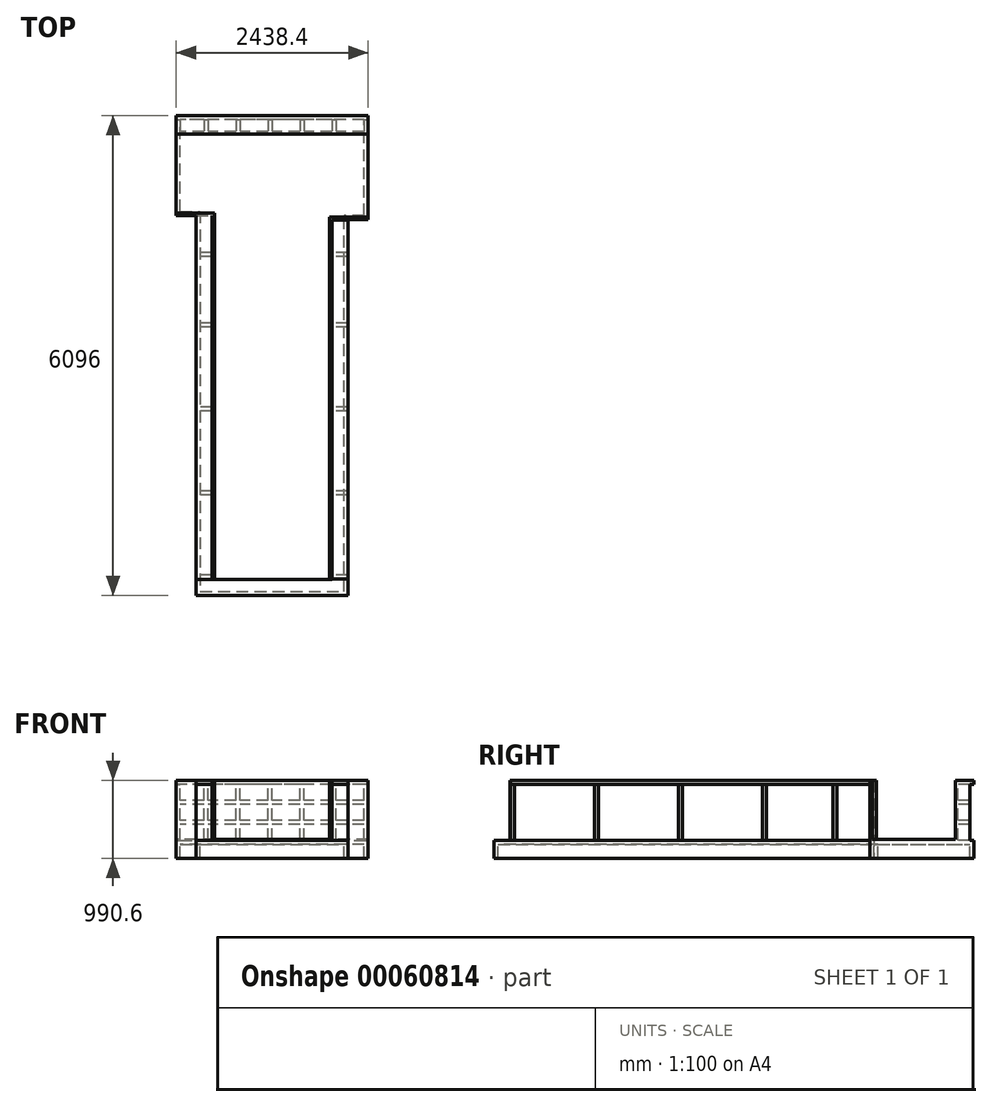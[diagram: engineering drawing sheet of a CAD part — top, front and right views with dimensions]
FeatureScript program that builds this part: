
annotation { "Feature Type Name" : "Feature", "Feature Type Description" : "" }
export const myFeature = defineFeature(function(context is Context, id is Id, definition is map)
    precondition{}
    {
        {
            var Q0;
            Q0=qCreatedBy(makeId("Top.planeOp"),FACE);
            var sketch = newSketch(context, id + "F0", { "sketchPlane" : qUnion([Q0])});
            skLineSegment(sketch, "E0", {"start": v(-1257.09, 0) * mm, "end": v(-1257.09, 1066.8) * mm});
            skLineSegment(sketch, "E1", {"start": v(-1257.09, 1066.8) * mm, "end": v(1181.31, 1066.8) * mm});
            skLineSegment(sketch, "E2", {"start": v(1181.31, 1066.8) * mm, "end": v(1181.31, -50.8) * mm});
            skLineSegment(sketch, "E3", {"start": v(1181.31, -50.8) * mm, "end": v(724.11, -50.8) * mm});
            skLineSegment(sketch, "E4", {"start": v(724.11, -50.8) * mm, "end": v(724.11, -4622.8) * mm});
            skLineSegment(sketch, "E5", {"start": v(724.11, -4622.8) * mm, "end": v(-799.89, -4622.8) * mm});
            skLineSegment(sketch, "E6", {"start": v(-1257.09, 0) * mm, "end": v(-799.89, 0) * mm});
            skLineSegment(sketch, "E7", {"start": v(-799.89, 0) * mm, "end": v(-799.89, -4622.8) * mm});
            skSolve(sketch);
        }
        {
            var Q0;
            Q0=qSketchRegion(id+"F0",true);
            extrude(context, id + "F1", {"entities" : qUnion([Q0]), "depth" : 12.7 * mm});
        }
        {
            var Q0;
            Q0=makeQuery(id+"F1.opExtrude","CAP_FACE",FACE,{"disambiguationData":[OSD([sQuery(id+"F0.wireOp",EDGE,"E0"),sQuery(id+"F0.wireOp",EDGE,"E1"),sQuery(id+"F0.wireOp",EDGE,"E2"),sQuery(id+"F0.wireOp",EDGE,"E3"),sQuery(id+"F0.wireOp",EDGE,"E4"),sQuery(id+"F0.wireOp",EDGE,"E5"),sQuery(id+"F0.wireOp",EDGE,"E6"),sQuery(id+"F0.wireOp",EDGE,"E7")])],"isStart":false});
            var sketch = newSketch(context, id + "F2", { "sketchPlane" : qUnion([Q0])});
            skLineSegment(sketch, "E8.0", {"start": v(-768.14, 31.75) * mm, "end": v(-1225.34, 31.75) * mm});
            skLineSegment(sketch, "E8.1", {"start": v(-768.14, -4591.05) * mm, "end": v(-768.14, 31.75) * mm});
            skLineSegment(sketch, "E8.2", {"start": v(-1225.34, 1035.05) * mm, "end": v(-1225.34, 31.75) * mm});
            skLineSegment(sketch, "E8.3", {"start": v(-768.14, -4591.05) * mm, "end": v(692.36, -4591.05) * mm});
            skLineSegment(sketch, "E8.4", {"start": v(1149.56, 1035.05) * mm, "end": v(-1225.34, 1035.05) * mm});
            skLineSegment(sketch, "E8.5", {"start": v(1149.56, -19.05) * mm, "end": v(1149.56, 1035.05) * mm});
            skLineSegment(sketch, "E8.6", {"start": v(692.36, -19.05) * mm, "end": v(1149.56, -19.05) * mm});
            skLineSegment(sketch, "E8.7", {"start": v(692.36, -4591.05) * mm, "end": v(692.36, -19.05) * mm});
            skLineSegment(sketch, "E9.0", {"start": v(-1257.09, 1066.8) * mm, "end": v(-1257.09, 0) * mm});
            skLineSegment(sketch, "E10.0", {"start": v(-799.89, 0) * mm, "end": v(-1257.09, 0) * mm});
            skLineSegment(sketch, "E11.0", {"start": v(-799.89, -4622.8) * mm, "end": v(-799.89, 0) * mm});
            skLineSegment(sketch, "E12.0", {"start": v(-799.89, -4622.8) * mm, "end": v(724.11, -4622.8) * mm});
            skLineSegment(sketch, "E13.0", {"start": v(724.11, -4622.8) * mm, "end": v(724.11, -50.8) * mm});
            skLineSegment(sketch, "E14.0", {"start": v(724.11, -50.8) * mm, "end": v(1181.31, -50.8) * mm});
            skLineSegment(sketch, "E15.0", {"start": v(1181.31, -50.8) * mm, "end": v(1181.31, 1066.8) * mm});
            skLineSegment(sketch, "E16.0", {"start": v(1181.31, 1066.8) * mm, "end": v(-1257.09, 1066.8) * mm});
            skSolve(sketch);
        }
        {
            var Q0;
            Q0=makeQuery(id+"F2.imprint","IMPRINT",FACE,{"disambiguationData":[TD([[makeQuery(id+"F2.imprint","IMPRINT",EDGE,{"derivedFrom":sQuery(id+"F2.wireOp",EDGE,"E8.0")}),1.0]])]});
            extrude(context, id + "F3", {"entities" : qUnion([Q0]), "operationType" : NewBodyOperationType.ADD, "depth" : 749.3 * mm});
        }
        {
            var Q0;
            Q0=makeQuery(id+"F0.imprint","IMPRINT",FACE,{"disambiguationData":[TD([[makeQuery(id+"F0.imprint","IMPRINT",EDGE,{"derivedFrom":sQuery(id+"F0.wireOp",EDGE,"E0")}),-1.0]])]});
            var sketch = newSketch(context, id + "F4", { "sketchPlane" : qUnion([Q0])});
            skLineSegment(sketch, "E17", {"start": v(927.31, -4826) * mm, "end": v(927.31, -50.8) * mm});
            skLineSegment(sketch, "E18", {"start": v(927.31, 1270) * mm, "end": v(-1003.09, 1270) * mm});
            skLineSegment(sketch, "E19", {"start": v(-1003.09, 0) * mm, "end": v(-1003.09, -4826) * mm});
            skLineSegment(sketch, "E20", {"start": v(-1003.09, -4826) * mm, "end": v(927.31, -4826) * mm});
            skLineSegment(sketch, "E21", {"start": v(-1003.09, 0) * mm, "end": v(-1257.09, 0) * mm});
            skLineSegment(sketch, "E22", {"start": v(-1257.09, 0) * mm, "end": v(-1257.09, 1270) * mm});
            skLineSegment(sketch, "E23", {"start": v(-1257.09, 1270) * mm, "end": v(-1003.09, 1270) * mm});
            skLineSegment(sketch, "E24", {"start": v(927.31, -50.8) * mm, "end": v(1181.31, -50.8) * mm});
            skLineSegment(sketch, "E25", {"start": v(1181.31, -50.8) * mm, "end": v(1181.31, 1270) * mm});
            skLineSegment(sketch, "E26", {"start": v(1181.31, 1270) * mm, "end": v(927.31, 1270) * mm});
            skSolve(sketch);
        }
        {
            var Q0;
            Q0=qSketchRegion(id+"F4",true);
            extrude(context, id + "F5", {"entities" : qUnion([Q0]), "operationType" : NewBodyOperationType.ADD, "oppositeDirection" : true, "depth" : 50.8 * mm});
        }
        {
            var Q0;
            Q0=makeQuery(id+"F3.boolean.opBoolean","MERGE",FACE,{"derivedFrom":[makeQuery(id+"F1.opExtrude","SWEPT_FACE",FACE,{"disambiguationData":[OSD([sQuery(id+"F0.wireOp",EDGE,"E1")])]}),makeQuery(id+"F3.opExtrude","SWEPT_FACE",FACE,{"disambiguationData":[OSD([sQuery(id+"F2.wireOp",EDGE,"E16.0")])]})]});
            var sketch = newSketch(context, id + "F6", { "sketchPlane" : qUnion([Q0])});
            skLineSegment(sketch, "E27.bottom", {"start": v(-1181.31, 0) * mm, "end": v(-1130.51, 0) * mm});
            skLineSegment(sketch, "E27.top", {"start": v(-1181.31, 711.2) * mm, "end": v(-1130.51, 711.2) * mm});
            skLineSegment(sketch, "E27.left", {"start": v(-1181.31, 0) * mm, "end": v(-1181.31, 711.2) * mm});
            skLineSegment(sketch, "E27.right", {"start": v(-1130.51, 0) * mm, "end": v(-1130.51, 203.2) * mm});
            skLineSegment(sketch, "E28.1.0.0", {"start": v(-774.91, 0) * mm, "end": v(-774.91, 203.2) * mm});
            skLineSegment(sketch, "E28.1.0.1", {"start": v(-724.11, 0) * mm, "end": v(-724.11, 203.2) * mm});
            skLineSegment(sketch, "E28.1.0.2", {"start": v(-774.91, 711.2) * mm, "end": v(-724.11, 711.2) * mm});
            skLineSegment(sketch, "E28.1.0.3", {"start": v(-774.91, 0) * mm, "end": v(-724.11, 0) * mm});
            skLineSegment(sketch, "E28.2.0.0", {"start": v(-368.51, 0) * mm, "end": v(-368.51, 203.2) * mm});
            skLineSegment(sketch, "E28.2.0.1", {"start": v(-317.71, 0) * mm, "end": v(-317.71, 203.2) * mm});
            skLineSegment(sketch, "E28.2.0.2", {"start": v(-368.51, 711.2) * mm, "end": v(-317.71, 711.2) * mm});
            skLineSegment(sketch, "E28.2.0.3", {"start": v(-368.51, 0) * mm, "end": v(-317.71, 0) * mm});
            skLineSegment(sketch, "E28.3.0.0", {"start": v(37.89, 0) * mm, "end": v(37.89, 203.2) * mm});
            skLineSegment(sketch, "E28.3.0.1", {"start": v(88.69, 0) * mm, "end": v(88.69, 203.2) * mm});
            skLineSegment(sketch, "E28.3.0.2", {"start": v(37.89, 711.2) * mm, "end": v(88.69, 711.2) * mm});
            skLineSegment(sketch, "E28.3.0.3", {"start": v(37.89, 0) * mm, "end": v(88.69, 0) * mm});
            skLineSegment(sketch, "E28.4.0.0", {"start": v(444.29, 0) * mm, "end": v(444.29, 203.2) * mm});
            skLineSegment(sketch, "E28.4.0.1", {"start": v(495.09, 0) * mm, "end": v(495.09, 203.2) * mm});
            skLineSegment(sketch, "E28.4.0.2", {"start": v(444.29, 711.2) * mm, "end": v(495.09, 711.2) * mm});
            skLineSegment(sketch, "E28.4.0.3", {"start": v(444.29, 0) * mm, "end": v(495.09, 0) * mm});
            skLineSegment(sketch, "E28.5.0.0", {"start": v(850.69, 0) * mm, "end": v(850.69, 203.2) * mm});
            skLineSegment(sketch, "E28.5.0.1", {"start": v(901.49, 0) * mm, "end": v(901.49, 203.2) * mm});
            skLineSegment(sketch, "E28.5.0.2", {"start": v(850.69, 711.2) * mm, "end": v(901.49, 711.2) * mm});
            skLineSegment(sketch, "E28.5.0.3", {"start": v(850.69, 0) * mm, "end": v(901.49, 0) * mm});
            skLineSegment(sketch, "E28.direction1", {"start": v(-1181.31, 0) * mm, "end": v(-774.91, 0) * mm, "construction": true});
            skLineSegment(sketch, "E29.bottom", {"start": v(1257.09, 0) * mm, "end": v(1206.29, 0) * mm});
            skLineSegment(sketch, "E29.top", {"start": v(1257.09, 711.2) * mm, "end": v(1206.29, 711.2) * mm});
            skLineSegment(sketch, "E29.left", {"start": v(1257.09, 0) * mm, "end": v(1257.09, 711.2) * mm});
            skLineSegment(sketch, "E29.right", {"start": v(1206.29, 0) * mm, "end": v(1206.29, 203.2) * mm});
            skLineSegment(sketch, "E30.bottom", {"start": v(-1130.51, 254) * mm, "end": v(-774.91, 254) * mm});
            skLineSegment(sketch, "E30.top", {"start": v(-1130.51, 203.2) * mm, "end": v(-774.91, 203.2) * mm});
            skLineSegment(sketch, "E30.left", {"start": v(-1181.31, 254) * mm, "end": v(-1181.31, 203.2) * mm});
            skLineSegment(sketch, "E30.right", {"start": v(1257.09, 254) * mm, "end": v(1257.09, 203.2) * mm});
            skLineSegment(sketch, "E31.bottom", {"start": v(-1130.51, 457.2) * mm, "end": v(-774.91, 457.2) * mm});
            skLineSegment(sketch, "E31.top", {"start": v(-1130.51, 508) * mm, "end": v(-774.91, 508) * mm});
            skLineSegment(sketch, "E31.left", {"start": v(-1181.31, 457.2) * mm, "end": v(-1181.31, 508) * mm});
            skLineSegment(sketch, "E31.right", {"start": v(1257.09, 457.2) * mm, "end": v(1257.09, 508) * mm});
            skLineSegment(sketch, "E32.trimOffspring", {"start": v(-1130.51, 508) * mm, "end": v(-1130.51, 711.2) * mm});
            skLineSegment(sketch, "E33.trimOffspring", {"start": v(-1130.51, 254) * mm, "end": v(-1130.51, 457.2) * mm});
            skLineSegment(sketch, "E34.trimOffspring", {"start": v(-774.91, 254) * mm, "end": v(-774.91, 457.2) * mm});
            skLineSegment(sketch, "E35.trimOffspring", {"start": v(-724.11, 254) * mm, "end": v(-368.51, 254) * mm});
            skLineSegment(sketch, "E36.trimOffspring", {"start": v(-724.11, 254) * mm, "end": v(-724.11, 457.2) * mm});
            skLineSegment(sketch, "E37.trimOffspring", {"start": v(-724.11, 203.2) * mm, "end": v(-368.51, 203.2) * mm});
            skLineSegment(sketch, "E38.trimOffspring", {"start": v(-724.11, 457.2) * mm, "end": v(-368.51, 457.2) * mm});
            skLineSegment(sketch, "E39.trimOffspring", {"start": v(-774.91, 508) * mm, "end": v(-774.91, 711.2) * mm});
            skLineSegment(sketch, "E40.trimOffspring", {"start": v(-724.11, 508) * mm, "end": v(-368.51, 508) * mm});
            skLineSegment(sketch, "E41.trimOffspring", {"start": v(-724.11, 508) * mm, "end": v(-724.11, 711.2) * mm});
            skLineSegment(sketch, "E42.trimOffspring", {"start": v(-368.51, 508) * mm, "end": v(-368.51, 711.2) * mm});
            skLineSegment(sketch, "E43.trimOffspring", {"start": v(-317.71, 508) * mm, "end": v(37.89, 508) * mm});
            skLineSegment(sketch, "E44.trimOffspring", {"start": v(-317.71, 508) * mm, "end": v(-317.71, 711.2) * mm});
            skLineSegment(sketch, "E45.trimOffspring", {"start": v(-317.71, 457.2) * mm, "end": v(37.89, 457.2) * mm});
            skLineSegment(sketch, "E46.trimOffspring", {"start": v(-317.71, 254) * mm, "end": v(37.89, 254) * mm});
            skLineSegment(sketch, "E47.trimOffspring", {"start": v(-368.51, 254) * mm, "end": v(-368.51, 457.2) * mm});
            skLineSegment(sketch, "E48.trimOffspring", {"start": v(-317.71, 203.2) * mm, "end": v(37.89, 203.2) * mm});
            skLineSegment(sketch, "E49.trimOffspring", {"start": v(-317.71, 254) * mm, "end": v(-317.71, 457.2) * mm});
            skLineSegment(sketch, "E50.trimOffspring", {"start": v(37.89, 254) * mm, "end": v(37.89, 457.2) * mm});
            skLineSegment(sketch, "E51.trimOffspring", {"start": v(88.69, 254) * mm, "end": v(444.29, 254) * mm});
            skLineSegment(sketch, "E52.trimOffspring", {"start": v(88.69, 254) * mm, "end": v(88.69, 457.2) * mm});
            skLineSegment(sketch, "E53.trimOffspring", {"start": v(88.69, 203.2) * mm, "end": v(444.29, 203.2) * mm});
            skLineSegment(sketch, "E54.trimOffspring", {"start": v(88.69, 457.2) * mm, "end": v(444.29, 457.2) * mm});
            skLineSegment(sketch, "E55.trimOffspring", {"start": v(37.89, 508) * mm, "end": v(37.89, 711.2) * mm});
            skLineSegment(sketch, "E56.trimOffspring", {"start": v(88.69, 508) * mm, "end": v(444.29, 508) * mm});
            skLineSegment(sketch, "E57.trimOffspring", {"start": v(88.69, 508) * mm, "end": v(88.69, 711.2) * mm});
            skLineSegment(sketch, "E58.trimOffspring", {"start": v(444.29, 508) * mm, "end": v(444.29, 711.2) * mm});
            skLineSegment(sketch, "E59.trimOffspring", {"start": v(495.09, 508) * mm, "end": v(495.09, 711.2) * mm});
            skLineSegment(sketch, "E60.trimOffspring", {"start": v(495.09, 457.2) * mm, "end": v(850.69, 457.2) * mm});
            skLineSegment(sketch, "E61.trimOffspring", {"start": v(495.09, 254) * mm, "end": v(850.69, 254) * mm});
            skLineSegment(sketch, "E62.trimOffspring", {"start": v(444.29, 254) * mm, "end": v(444.29, 457.2) * mm});
            skLineSegment(sketch, "E63.trimOffspring", {"start": v(495.09, 203.2) * mm, "end": v(850.69, 203.2) * mm});
            skLineSegment(sketch, "E64.trimOffspring", {"start": v(495.09, 254) * mm, "end": v(495.09, 457.2) * mm});
            skLineSegment(sketch, "E65.trimOffspring", {"start": v(850.69, 254) * mm, "end": v(850.69, 457.2) * mm});
            skLineSegment(sketch, "E66.trimOffspring", {"start": v(901.49, 254) * mm, "end": v(901.49, 457.2) * mm});
            skLineSegment(sketch, "E67.trimOffspring", {"start": v(901.49, 254) * mm, "end": v(1206.29, 254) * mm});
            skLineSegment(sketch, "E68.trimOffspring", {"start": v(901.49, 203.2) * mm, "end": v(1206.29, 203.2) * mm});
            skLineSegment(sketch, "E69.trimOffspring", {"start": v(901.49, 457.2) * mm, "end": v(1206.29, 457.2) * mm});
            skLineSegment(sketch, "E70.trimOffspring", {"start": v(901.49, 508) * mm, "end": v(1206.29, 508) * mm});
            skLineSegment(sketch, "E71", {"start": v(495.09, 508) * mm, "end": v(850.69, 508) * mm});
            skPoint(sketch, "E71.endSnap0", {"position": v(850.69, 482.6) * mm});
            skLineSegment(sketch, "E72.trimOffspring", {"start": v(850.69, 508) * mm, "end": v(850.69, 711.2) * mm});
            skLineSegment(sketch, "E73.trimOffspring", {"start": v(901.49, 508) * mm, "end": v(901.49, 711.2) * mm});
            skLineSegment(sketch, "E74.trimOffspring", {"start": v(1206.29, 254) * mm, "end": v(1206.29, 457.2) * mm});
            skLineSegment(sketch, "E75.trimOffspring", {"start": v(1206.29, 508) * mm, "end": v(1206.29, 711.2) * mm});
            skSolve(sketch);
        }
        {
            var Q0;
            Q0=qSketchRegion(id+"F6",true);
            extrude(context, id + "F7", {"entities" : qUnion([Q0]), "operationType" : NewBodyOperationType.ADD, "depth" : 152.4 * mm});
        }
        {
            var Q0;
            {var subQ1=sQuery(id+"F2.wireOp",EDGE,"E16.0");Q0=makeQuery(id+"F7.boolean.opBoolean","SPLIT",FACE,{"disambiguationData":[TD([makeQuery(id+"F1.opExtrude","SWEPT_FACE",FACE,{"disambiguationData":[OSD([sQuery(id+"F0.wireOp",EDGE,"E0")])]})])],"derivedFrom":makeQuery(id+"F3.boolean.opBoolean","MERGE",FACE,{"derivedFrom":[makeQuery(id+"F1.opExtrude","SWEPT_FACE",FACE,{"disambiguationData":[OSD([sQuery(id+"F0.wireOp",EDGE,"E1")])]}),makeQuery(id+"F3.opExtrude","SWEPT_FACE",FACE,{"disambiguationData":[OSD([subQ1])]})]})});}
            var sketch = newSketch(context, id + "F8", { "sketchPlane" : qUnion([Q0])});
            skLineSegment(sketch, "E76.bottom", {"start": v(-1181.31, 762) * mm, "end": v(1257.09, 762) * mm});
            skLineSegment(sketch, "E76.top", {"start": v(-1181.31, 711.2) * mm, "end": v(1257.09, 711.2) * mm});
            skLineSegment(sketch, "E76.left", {"start": v(-1181.31, 762) * mm, "end": v(-1181.31, 711.2) * mm});
            skLineSegment(sketch, "E76.right", {"start": v(1257.09, 762) * mm, "end": v(1257.09, 711.2) * mm});
            skSolve(sketch);
        }
        {
            var Q0;
            Q0 = qSketchRegion(id + "F8", true);
            extrude(context, id + "F9", {"entities" : qUnion([Q0]), "operationType" : NewBodyOperationType.ADD, "depth" : 203.2 * mm});
        }
        {
            var Q0;
            Q0=makeQuery(id+"F3.opExtrude","SWEPT_FACE",FACE,{"disambiguationData":[OSD([sQuery(id+"F2.wireOp",EDGE,"E8.5")])]});
            var sketch = newSketch(context, id + "F10", { "sketchPlane" : qUnion([Q0])});
            skLineSegment(sketch, "E77.0", {"start": v(19.05, 12.7) * mm, "end": v(-1035.05, 12.7) * mm});
            skLineSegment(sketch, "E78.0", {"start": v(19.05, 762) * mm, "end": v(19.05, 12.7) * mm});
            skLineSegment(sketch, "E79.0", {"start": v(-1035.05, 762) * mm, "end": v(-1035.05, 12.7) * mm});
            skLineSegment(sketch, "E80.0", {"start": v(19.05, 762) * mm, "end": v(-1035.05, 762) * mm});
            skSolve(sketch);
        }
        {
            var Q0;
            Q0 = qSketchRegion(id + "F10", true);
            extrude(context, id + "F11", {"entities" : qUnion([Q0]), "operationType" : NewBodyOperationType.REMOVE, "endBound" : BoundingType.THROUGH_ALL, "oppositeDirection" : true, "depth" : 25.4 * mm});
        }
        {
            var Q0;
            Q0=makeQuery(id+"F3.opExtrude","SWEPT_FACE",FACE,{"disambiguationData":[OSD([sQuery(id+"F2.wireOp",EDGE,"E8.2")])]});
            var sketch = newSketch(context, id + "F12", { "sketchPlane" : qUnion([Q0])});
            skLineSegment(sketch, "E81.0", {"start": v(1035.05, 762) * mm, "end": v(31.75, 762) * mm});
            skLineSegment(sketch, "E82.0", {"start": v(31.75, 762) * mm, "end": v(31.75, 12.7) * mm});
            skLineSegment(sketch, "E83.0", {"start": v(1035.05, 12.7) * mm, "end": v(31.75, 12.7) * mm});
            skLineSegment(sketch, "E84.0", {"start": v(1035.05, 762) * mm, "end": v(1035.05, 12.7) * mm});
            skSolve(sketch);
        }
        {
            var Q0;
            Q0 = qSketchRegion(id + "F12", true);
            extrude(context, id + "F13", {"entities" : qUnion([Q0]), "operationType" : NewBodyOperationType.REMOVE, "endBound" : BoundingType.THROUGH_ALL, "oppositeDirection" : true, "depth" : 25.4 * mm});
        }
        {
            var Q0;
            Q0=makeQuery(id+"F3.opExtrude","SWEPT_FACE",FACE,{"disambiguationData":[OSD([sQuery(id+"F2.wireOp",EDGE,"E8.3")])]});
            var sketch = newSketch(context, id + "F14", { "sketchPlane" : qUnion([Q0])});
            skLineSegment(sketch, "E85.0", {"start": v(-692.36, 762) * mm, "end": v(-692.36, 12.7) * mm});
            skLineSegment(sketch, "E86.0", {"start": v(768.14, 762) * mm, "end": v(-692.36, 762) * mm});
            skLineSegment(sketch, "E87.0", {"start": v(768.14, 762) * mm, "end": v(768.14, 12.7) * mm});
            skLineSegment(sketch, "E88.0", {"start": v(768.14, 12.7) * mm, "end": v(-692.36, 12.7) * mm});
            skSolve(sketch);
        }
        {
            var Q0;
            Q0 = qSketchRegion(id + "F14", true);
            extrude(context, id + "F15", {"entities" : qUnion([Q0]), "operationType" : NewBodyOperationType.REMOVE, "endBound" : BoundingType.THROUGH_ALL, "oppositeDirection" : true, "depth" : 25.4 * mm});
        }
        {
            var Q0;
            {var subQ0=sQuery(id+"F4.wireOp",EDGE,"E24");var subQ1=sQuery(id+"F4.wireOp",EDGE,"E17");var subQ2=sQuery(id+"F4.wireOp",EDGE,"E19");var subQ3=sQuery(id+"F4.wireOp",EDGE,"E20");var subQ4=sQuery(id+"F4.wireOp",EDGE,"E21");Q0=makeQuery(id+"F5.boolean.opBoolean","SPLIT",FACE,{"disambiguationData":[TD([makeQuery(id+"F1.opExtrude","SWEPT_FACE",FACE,{"disambiguationData":[OSD([sQuery(id+"F0.wireOp",EDGE,"E3")])]})])],"derivedFrom":makeQuery(id+"F5.opExtrude","CAP_FACE",FACE,{"disambiguationData":[OSD([subQ1,sQuery(id+"F4.wireOp",EDGE,"E18"),subQ2,subQ3,subQ4,sQuery(id+"F4.wireOp",EDGE,"E22"),sQuery(id+"F4.wireOp",EDGE,"E23"),subQ0,sQuery(id+"F4.wireOp",EDGE,"E25"),sQuery(id+"F4.wireOp",EDGE,"E26")])],"isStart":true})});}
            var sketch = newSketch(context, id + "F16", { "sketchPlane" : qUnion([Q0])});
            skPoint(sketch, "E89.0.end.orphan", {"position": v(873.68, -4569.35) * mm});
            skPoint(sketch, "E89.0.start.orphan", {"position": v(-15.32, -4569.35) * mm});
            skLineSegment(sketch, "E90.bottom", {"start": v(924.48, -4569.35) * mm, "end": v(-1005.92, -4569.35) * mm});
            skLineSegment(sketch, "E90.top", {"start": v(924.48, -4620.15) * mm, "end": v(-1005.92, -4620.15) * mm});
            skLineSegment(sketch, "E91.bottom", {"start": v(924.48, -3553.35) * mm, "end": v(-1005.92, -3553.35) * mm});
            skLineSegment(sketch, "E91.top", {"start": v(924.48, -3502.55) * mm, "end": v(-1005.92, -3502.55) * mm});
            skLineSegment(sketch, "E92.bottom", {"start": v(-103.03, -1419.75) * mm, "end": v(-1005.92, -1419.75) * mm});
            skLineSegment(sketch, "E92.top", {"start": v(924.48, -1368.95) * mm, "end": v(-1005.92, -1368.95) * mm});
            skLineSegment(sketch, "E93.bottom", {"start": v(924.48, -473.6) * mm, "end": v(-1005.92, -473.6) * mm});
            skLineSegment(sketch, "E93.top", {"start": v(924.48, -524.4) * mm, "end": v(-1005.92, -524.4) * mm});
            skLineSegment(sketch, "E94.bottom", {"start": v(924.48, -2486.55) * mm, "end": v(-1005.92, -2486.55) * mm});
            skLineSegment(sketch, "E94.top", {"start": v(924.48, -2435.75) * mm, "end": v(-1005.92, -2435.75) * mm});
            skPoint(sketch, "E95.0.end.orphan", {"position": v(873.68, -2486.55) * mm});
            skPoint(sketch, "E95.0.start.orphan", {"position": v(-15.32, -2486.55) * mm});
            skPoint(sketch, "E96.0.end.orphan", {"position": v(873.68, -3553.35) * mm});
            skPoint(sketch, "E96.0.start.orphan", {"position": v(-15.32, -3553.35) * mm});
            skLineSegment(sketch, "E91.right", {"start": v(-1005.92, -3553.35) * mm, "end": v(-1005.92, -3502.55) * mm});
            skLineSegment(sketch, "E90.right", {"start": v(-1005.92, -4569.35) * mm, "end": v(-1005.92, -4620.15) * mm});
            skLineSegment(sketch, "E94.right", {"start": v(-1005.92, -2486.55) * mm, "end": v(-1005.92, -2435.75) * mm});
            skLineSegment(sketch, "E97.0", {"start": v(721.28, -505.35) * mm, "end": v(-802.72, -505.35) * mm});
            skLineSegment(sketch, "E98", {"start": v(-103.03, -1419.75) * mm, "end": v(924.48, -1419.75) * mm});
            skLineSegment(sketch, "E92.left", {"start": v(924.48, -1419.75) * mm, "end": v(924.48, -1368.95) * mm});
            skLineSegment(sketch, "E92.right", {"start": v(-1005.92, -1419.75) * mm, "end": v(-1005.92, -1368.95) * mm});
            skLineSegment(sketch, "E93.left", {"start": v(924.48, -473.6) * mm, "end": v(924.48, -524.4) * mm});
            skLineSegment(sketch, "E93.right", {"start": v(-1005.92, -473.6) * mm, "end": v(-1005.92, -524.4) * mm});
            skLineSegment(sketch, "E91.left", {"start": v(924.48, -3553.35) * mm, "end": v(924.48, -3502.55) * mm});
            skLineSegment(sketch, "E90.left", {"start": v(924.48, -4569.35) * mm, "end": v(924.48, -4620.15) * mm});
            skLineSegment(sketch, "E94.left", {"start": v(924.48, -2486.55) * mm, "end": v(924.48, -2435.75) * mm});
            skSolve(sketch);
        }
        {
            var Q0;
            Q0 = qSketchRegion(id + "F16", true);
            extrude(context, id + "F17", {"entities" : qUnion([Q0]), "operationType" : NewBodyOperationType.ADD, "depth" : 711.2 * mm});
        }
        {
            var Q0;
            {var subQ0=sQuery(id+"F16.wireOp",EDGE,"E93.bottom");Q0=makeQuery(id+"F17.boolean.opBoolean","SPLIT",FACE,{"disambiguationData":[TD([makeQuery(id+"F3.opExtrude","SWEPT_FACE",FACE,{"disambiguationData":[OSD([sQuery(id+"F2.wireOp",EDGE,"E8.1")])]})])],"derivedFrom":makeQuery(id+"F17.opExtrude","SWEPT_FACE",FACE,{"disambiguationData":[OSD([subQ0])]})});}
            var sketch = newSketch(context, id + "F18", { "sketchPlane" : qUnion([Q0])});
            skLineSegment(sketch, "E99.0", {"start": v(768.14, 12.7) * mm, "end": v(768.14, 711.2) * mm});
            skLineSegment(sketch, "E100.0", {"start": v(-692.36, 711.2) * mm, "end": v(768.14, 711.2) * mm});
            skLineSegment(sketch, "E101.0", {"start": v(768.14, 12.7) * mm, "end": v(-692.36, 12.7) * mm});
            skLineSegment(sketch, "E102.0", {"start": v(-692.36, 12.7) * mm, "end": v(-692.36, 711.2) * mm});
            skSolve(sketch);
        }
        {
            var Q0;
            Q0 = qSketchRegion(id + "F18", true);
            extrude(context, id + "F19", {"entities" : qUnion([Q0]), "operationType" : NewBodyOperationType.REMOVE, "endBound" : BoundingType.THROUGH_ALL, "oppositeDirection" : true, "depth" : 25.4 * mm});
        }
        {
            var Q0;
            {var subQ0=sQuery(id+"F16.wireOp",EDGE,"E91.bottom");var subQ1=sQuery(id+"F16.wireOp",EDGE,"E91.top");var subQ2=sQuery(id+"F16.wireOp",EDGE,"E91.right");Q0=makeQuery(id+"F17.boolean.opBoolean","SPLIT",FACE,{"disambiguationData":[TD([makeQuery(id+"F1.opExtrude","SWEPT_FACE",FACE,{"disambiguationData":[OSD([sQuery(id+"F0.wireOp",EDGE,"E7")])]})])],"derivedFrom":makeQuery(id+"F17.opExtrude","CAP_FACE",FACE,{"disambiguationData":[OSD([subQ0,subQ1,subQ2,sQuery(id+"F16.wireOp",EDGE,"E91.left")])],"isStart":false})});}
            var sketch = newSketch(context, id + "F20", { "sketchPlane" : qUnion([Q0])});
            skLineSegment(sketch, "E103.right", {"start": v(-1003.84, 0.44) * mm, "end": v(-1003.84, -4622.36) * mm});
            skLineSegment(sketch, "E104.right", {"start": v(928.59, -4618.25) * mm, "end": v(928.59, -55.1) * mm});
            skLineSegment(sketch, "E103.top", {"start": v(-800.64, -4622.36) * mm, "end": v(-1003.84, -4622.36) * mm});
            skLineSegment(sketch, "E103.left", {"start": v(-800.64, 0.44) * mm, "end": v(-800.64, -4622.36) * mm});
            skLineSegment(sketch, "E104.bottom", {"start": v(725.39, -4618.25) * mm, "end": v(928.59, -4618.25) * mm});
            skLineSegment(sketch, "E103.bottom", {"start": v(-800.64, 0.44) * mm, "end": v(-1003.84, 0.44) * mm});
            skLineSegment(sketch, "E104.left", {"start": v(725.39, -4618.25) * mm, "end": v(725.39, -55.1) * mm});
            skLineSegment(sketch, "E104.top", {"start": v(725.39, -55.1) * mm, "end": v(928.59, -55.1) * mm});
            skLineSegment(sketch, "E105.0", {"start": v(-1003.84, -4622.36) * mm, "end": v(-800.64, -4622.36) * mm});
            skSolve(sketch);
        }
        {
            var Q0;
            Q0 = qSketchRegion(id + "F20", true);
            var Q1;
            {var subQ0=sQuery(id+"F2.wireOp",EDGE,"E11.0");var subQ3=sQuery(id+"F2.wireOp",EDGE,"E9.0");var subQ5=sQuery(id+"F2.wireOp",EDGE,"E10.0");var subQ7=sQuery(id+"F2.wireOp",EDGE,"E8.0");var subQ9=makeQuery(id+"F1.opExtrude","SWEPT_FACE",FACE,{"disambiguationData":[OSD([sQuery(id+"F0.wireOp",EDGE,"E0")])]});var subQ11=sQuery(id+"F2.wireOp",EDGE,"E12.0");var subQ14=sQuery(id+"F2.wireOp",EDGE,"E8.1");var subQ21=sQuery(id+"F2.wireOp",EDGE,"E15.0");var subQ22=sQuery(id+"F2.wireOp",EDGE,"E13.0");var subQ23=sQuery(id+"F2.wireOp",EDGE,"E14.0");var subQ24=sQuery(id+"F2.wireOp",EDGE,"E8.6");var subQ25=sQuery(id+"F2.wireOp",EDGE,"E8.7");var subQ26=sQuery(id+"F2.wireOp",EDGE,"E8.3");Q1=makeQuery(id+"F15.boolean.opBoolean","SPLIT",FACE,{"disambiguationData":[TD([subQ9])],"derivedFrom":makeQuery(id+"F13.boolean.opBoolean","SPLIT",FACE,{"disambiguationData":[TD([makeQuery(id+"F1.opExtrude","SWEPT_FACE",FACE,{"disambiguationData":[OSD([sQuery(id+"F0.wireOp",EDGE,"E3")])]})])],"derivedFrom":makeQuery(id+"F9.boolean.opBoolean","MERGE",FACE,{"derivedFrom":[makeQuery(id+"F3.opExtrude","CAP_FACE",FACE,{"disambiguationData":[OSD([subQ7,subQ14,sQuery(id+"F2.wireOp",EDGE,"E8.2"),subQ26,sQuery(id+"F2.wireOp",EDGE,"E8.4"),sQuery(id+"F2.wireOp",EDGE,"E8.5"),subQ24,subQ25,subQ3,subQ5,subQ0,subQ11,subQ22,subQ23,subQ21,sQuery(id+"F2.wireOp",EDGE,"E16.0")])],"isStart":false}),makeQuery(id+"F9.opExtrude","SWEPT_FACE",FACE,{"disambiguationData":[OSD([sQuery(id+"F8.wireOp",EDGE,"E76.bottom")])]})]})})});}
            extrude(context, id + "F21", {"entities" : qUnion([Q0]), "operationType" : NewBodyOperationType.ADD, "endBound" : BoundingType.UP_TO_SURFACE, "endBoundEntityFace" : qUnion([Q1]), "depth" : 50.8 * mm});
        }
        {
            var Q0;
            Q0=makeQuery(id+"F5.opExtrude","CAP_FACE",FACE,{"disambiguationData":[OSD([sQuery(id+"F4.wireOp",EDGE,"E17"),sQuery(id+"F4.wireOp",EDGE,"E18"),sQuery(id+"F4.wireOp",EDGE,"E19"),sQuery(id+"F4.wireOp",EDGE,"E20"),sQuery(id+"F4.wireOp",EDGE,"E21"),sQuery(id+"F4.wireOp",EDGE,"E22"),sQuery(id+"F4.wireOp",EDGE,"E23"),sQuery(id+"F4.wireOp",EDGE,"E24"),sQuery(id+"F4.wireOp",EDGE,"E25"),sQuery(id+"F4.wireOp",EDGE,"E26")])],"isStart":false});
            var sketch = newSketch(context, id + "F22", { "sketchPlane" : qUnion([Q0])});
            skLineSegment(sketch, "E106.0", {"start": v(927.31, 4826) * mm, "end": v(927.31, 50.8) * mm});
            skLineSegment(sketch, "E107.0", {"start": v(-1003.09, 4826) * mm, "end": v(927.31, 4826) * mm});
            skLineSegment(sketch, "E108.0", {"start": v(-1003.09, 0) * mm, "end": v(-1003.09, 4826) * mm});
            skLineSegment(sketch, "E109.0", {"start": v(-1257.09, 0) * mm, "end": v(-1003.09, 0) * mm});
            skLineSegment(sketch, "E110.0", {"start": v(-1257.09, 0) * mm, "end": v(-1257.09, -1270) * mm});
            skLineSegment(sketch, "E111.0", {"start": v(1181.31, -1270) * mm, "end": v(-1257.09, -1270) * mm});
            skLineSegment(sketch, "E112.0", {"start": v(1181.31, 50.8) * mm, "end": v(1181.31, -1270) * mm});
            skLineSegment(sketch, "E113.0", {"start": v(1181.31, 50.8) * mm, "end": v(927.31, 50.8) * mm});
            skLineSegment(sketch, "E114.0", {"start": v(1130.51, 0) * mm, "end": v(1130.51, -1219.2) * mm});
            skLineSegment(sketch, "E114.1", {"start": v(1130.51, -1219.2) * mm, "end": v(-1206.29, -1219.2) * mm});
            skLineSegment(sketch, "E114.2", {"start": v(1130.51, 0) * mm, "end": v(876.51, 0) * mm});
            skLineSegment(sketch, "E114.3", {"start": v(-1206.29, -50.8) * mm, "end": v(-1206.29, -1219.2) * mm});
            skLineSegment(sketch, "E114.4", {"start": v(876.51, 4775.2) * mm, "end": v(876.51, 0) * mm});
            skLineSegment(sketch, "E114.5", {"start": v(-952.29, 4775.2) * mm, "end": v(876.51, 4775.2) * mm});
            skLineSegment(sketch, "E114.6", {"start": v(-952.29, -50.8) * mm, "end": v(-952.29, 4775.2) * mm});
            skLineSegment(sketch, "E114.7", {"start": v(-1206.29, -50.8) * mm, "end": v(-952.29, -50.8) * mm});
            skSolve(sketch);
        }
        {
            var Q0;
            Q0 = qSketchRegion(id + "F22", true);
            extrude(context, id + "F23", {"entities" : qUnion([Q0]), "operationType" : NewBodyOperationType.ADD, "depth" : 177.8 * mm});
        }
    });
